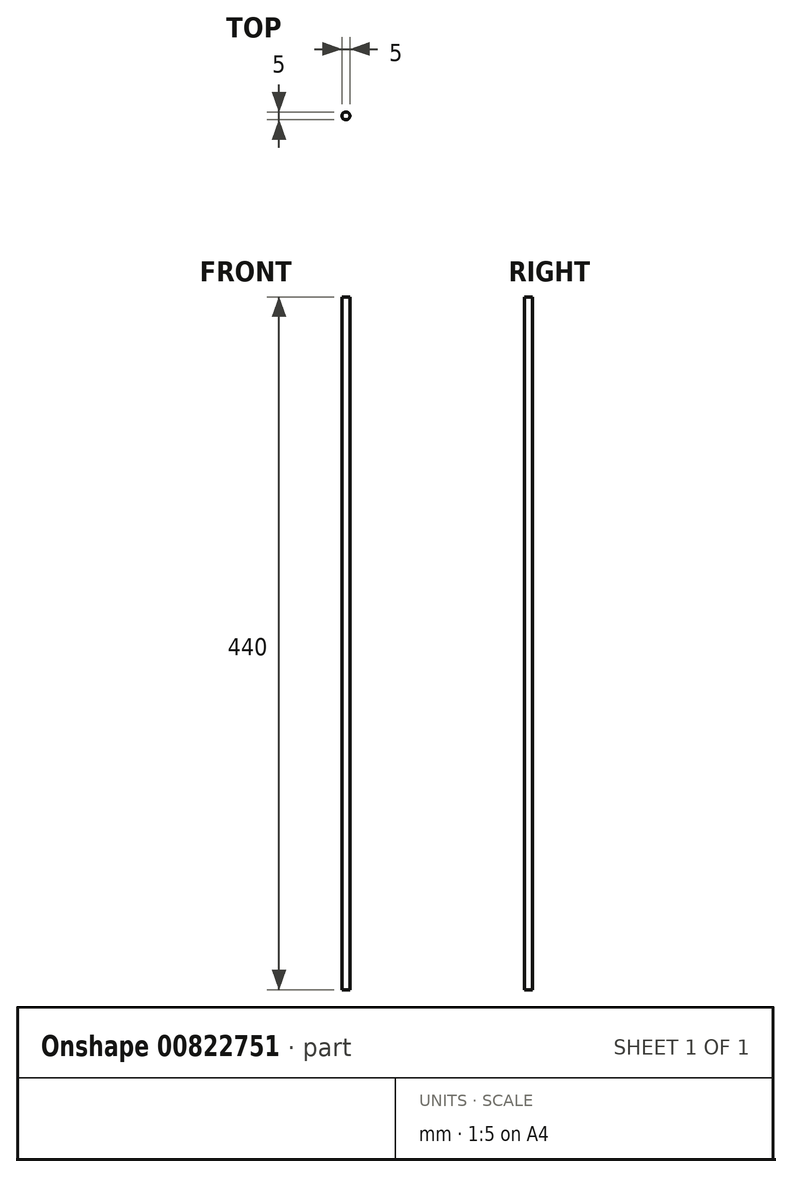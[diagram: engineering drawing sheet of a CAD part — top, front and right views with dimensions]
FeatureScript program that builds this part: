
annotation { "Feature Type Name" : "Feature", "Feature Type Description" : "" }
export const myFeature = defineFeature(function(context is Context, id is Id, definition is map)
    precondition{}
    {
        {
            assignVariable(context, id + "F0", {"name" : "length", "anyValue" : 440});
        }
        {
            var Q0;
            Q0=qCreatedBy(makeId("Top.planeOp"),FACE);
            var sketch = newSketch(context, id + "F1", { "sketchPlane" : qUnion([Q0])});
            skCircle(sketch, "E0", {"center": v(0, 0) * mm, "radius": 2.5 * mm});
            skSolve(sketch);
        }
        {
            var Q0;
            Q0=qSketchRegion(id+"F1",true);
            extrude(context, id + "F2", {"entities" : qUnion([Q0]), "depth" : (getVariable(context, 'length')) * mm, "offsetDistance" : 25 * mm});
        }
    });
